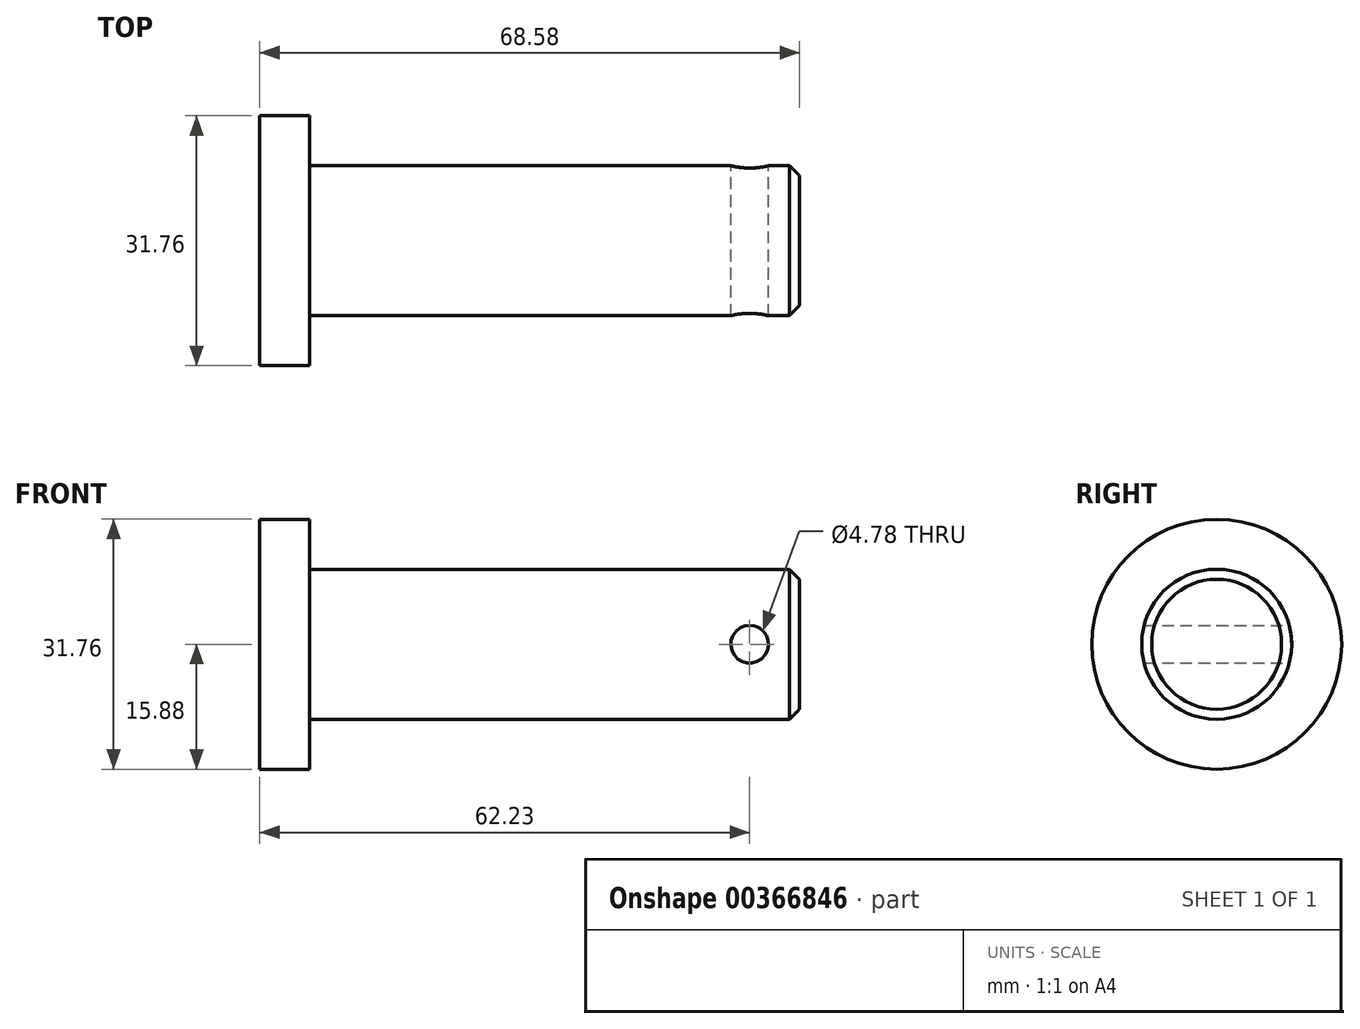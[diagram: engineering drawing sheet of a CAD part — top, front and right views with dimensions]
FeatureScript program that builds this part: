
annotation { "Feature Type Name" : "Feature", "Feature Type Description" : "" }
export const myFeature = defineFeature(function(context is Context, id is Id, definition is map)
    precondition{}
    {
        {
            var Q0;
            Q0=qCreatedBy(makeId("Right.planeOp"),FACE);
            var sketch = newSketch(context, id + "F0", { "sketchPlane" : qUnion([Q0])});
            skCircle(sketch, "E0", {"center": v(0, 0) * mm, "radius": 15.87 * mm});
            skSolve(sketch);
        }
        {
            var Q0;
            Q0 = qSketchRegion(id + "F0", true);
            extrude(context, id + "F1", {"entities" : qUnion([Q0]), "depth" : 6.35 * mm});
        }
        {
            var Q0;
            Q0=makeQuery(id+"F1.opExtrude","CAP_FACE",FACE,{"disambiguationData":[OSD([sQuery(id+"F0.wireOp",EDGE,"E0")])],"isStart":false});
            var sketch = newSketch(context, id + "F2", { "sketchPlane" : qUnion([Q0])});
            skCircle(sketch, "E1", {"center": v(0, 0) * mm, "radius": 9.53 * mm});
            skSolve(sketch);
        }
        {
            var Q0;
            Q0 = qSketchRegion(id + "F2", true);
            extrude(context, id + "F3", {"entities" : qUnion([Q0]), "operationType" : NewBodyOperationType.ADD, "depth" : 62.23 * mm});
        }
        {
            var Q0;
            Q0=qCreatedBy(makeId("Front.planeOp"),FACE);
            var sketch = newSketch(context, id + "F4", { "sketchPlane" : qUnion([Q0])});
            skCircle(sketch, "E2", {"center": v(62.23, 0) * mm, "radius": 2.39 * mm});
            skSolve(sketch);
        }
        {
            var Q0;
            Q0 = qSketchRegion(id + "F4", true);
            extrude(context, id + "F5", {"entities" : qUnion([Q0]), "operationType" : NewBodyOperationType.REMOVE, "endBound" : BoundingType.THROUGH_ALL, "depth" : 25.4 * mm, "hasSecondDirection" : true, "secondDirectionOppositeDirection" : true, "secondDirectionDepth" : 25.4 * mm});
        }
        {
            var Q0;
            Q0=makeQuery(id+"F3.opExtrude","CAP_EDGE",EDGE,{"disambiguationData":[OSD([sQuery(id+"F2.wireOp",EDGE,"E1")])],"isStart":false});
            chamfer(context, id + "F6", {"entities" : qUnion([Q0]), "chamferType" : ChamferType.OFFSET_ANGLE, "width" : 1.27 * mm, "oppositeDirection" : false, "angle" : 45 * degree, "tangentPropagation" : true});
        }
    });
